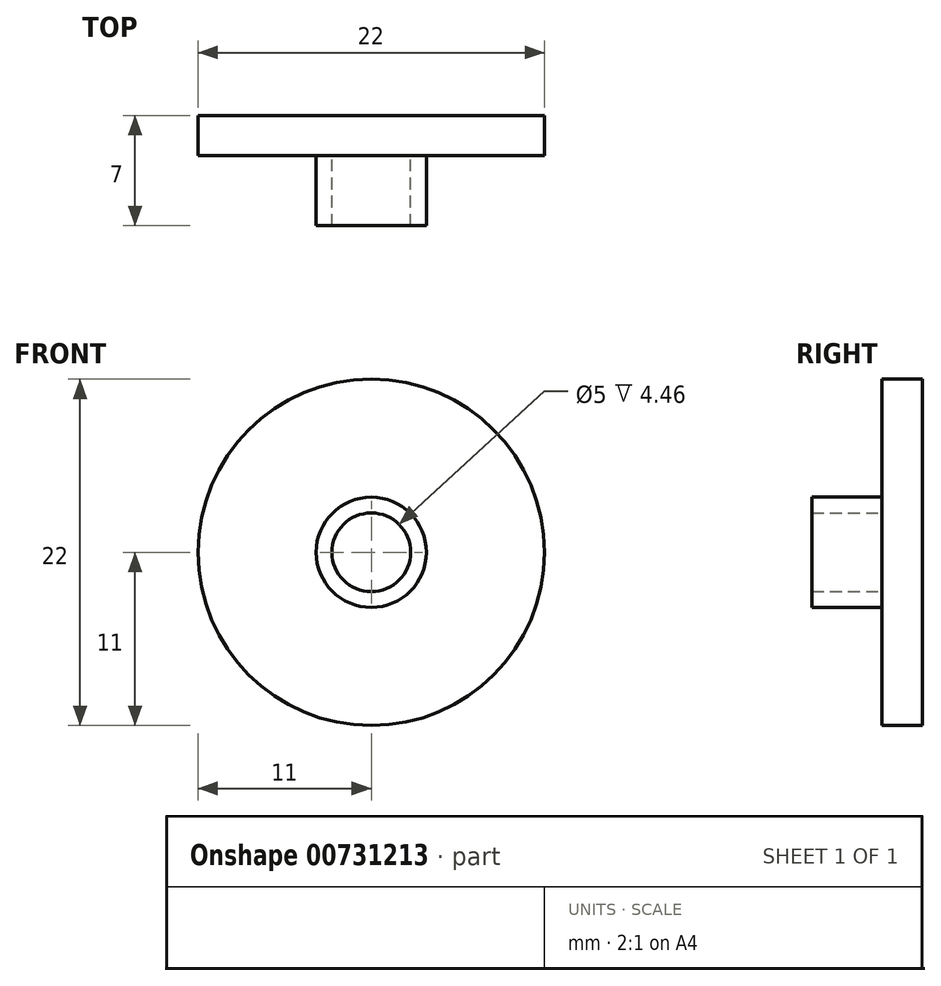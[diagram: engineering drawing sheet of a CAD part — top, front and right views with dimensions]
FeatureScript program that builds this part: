
annotation { "Feature Type Name" : "Feature", "Feature Type Description" : "" }
export const myFeature = defineFeature(function(context is Context, id is Id, definition is map)
    precondition{}
    {
        {
            var Q0;
            Q0=qCreatedBy(makeId("Front.planeOp"),FACE);
            var sketch = newSketch(context, id + "F0", { "sketchPlane" : qUnion([Q0])});
            skCircle(sketch, "E0", {"center": v(0, 0) * mm, "radius": 3.5 * mm});
            skCircle(sketch, "E1", {"center": v(0, 0) * mm, "radius": 2.5 * mm});
            skSolve(sketch);
        }
        {
            var Q0;
            Q0 = qSketchRegion(id + "F0", true);
            extrude(context, id + "F1", {"entities" : qUnion([Q0]), "depth" : 7 * mm, "offsetDistance" : 25.4 * mm});
        }
        {
            var Q0;
            Q0=qCreatedBy(makeId("Front.planeOp"),FACE);
            var sketch = newSketch(context, id + "F2", { "sketchPlane" : qUnion([Q0])});
            skCircle(sketch, "E2", {"center": v(0, 0) * mm, "radius": 11 * mm});
            skSolve(sketch);
        }
        {
            var Q0;
            Q0 = qSketchRegion(id + "F2", true);
            extrude(context, id + "F3", {"entities" : qUnion([Q0]), "operationType" : NewBodyOperationType.ADD, "depth" : 2.54 * mm, "offsetDistance" : 25.4 * mm});
        }
    });
